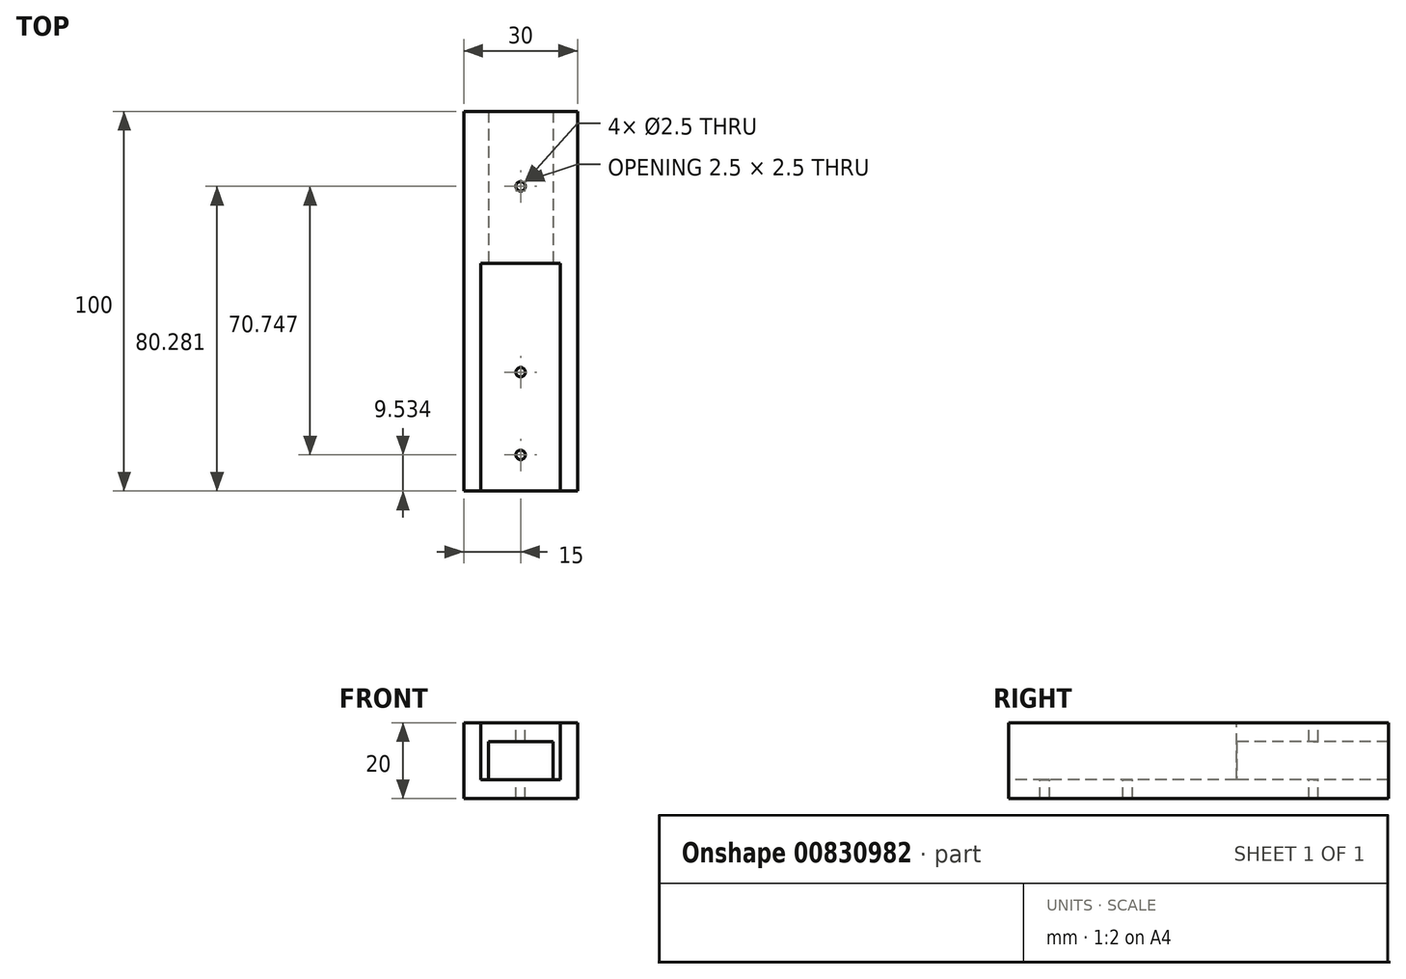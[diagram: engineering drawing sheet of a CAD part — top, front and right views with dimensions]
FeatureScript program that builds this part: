
annotation { "Feature Type Name" : "Feature", "Feature Type Description" : "" }
export const myFeature = defineFeature(function(context is Context, id is Id, definition is map)
    precondition{}
    {
        {
            var Q0;
            Q0=qCreatedBy(makeId("Top.planeOp"),FACE);
            var sketch = newSketch(context, id + "F0", { "sketchPlane" : qUnion([Q0])});
            skLineSegment(sketch, "E0.bottom", {"start": v(-15, 50) * mm, "end": v(15, 50) * mm});
            skLineSegment(sketch, "E0.top", {"start": v(-15, -50) * mm, "end": v(15, -50) * mm});
            skLineSegment(sketch, "E0.left", {"start": v(-15, 50) * mm, "end": v(-15, -50) * mm});
            skLineSegment(sketch, "E0.right", {"start": v(15, 50) * mm, "end": v(15, -50) * mm});
            skPoint(sketch, "E0.middle", {"position": v(0, 0) * mm});
            skSolve(sketch);
        }
        {
            var Q0;
            Q0 = qSketchRegion(id + "F0", true);
            extrude(context, id + "F1", {"entities" : qUnion([Q0]), "endBound" : BoundingType.SYMMETRIC, "depth" : 20 * mm, "offsetDistance" : 25 * mm});
        }
        {
            var Q0;
            Q0=makeQuery(id+"F1.opExtrude","SWEPT_FACE",FACE,{"disambiguationData":[OSD([sQuery(id+"F0.wireOp",EDGE,"E0.top")])]});
            var sketch = newSketch(context, id + "F2", { "sketchPlane" : qUnion([Q0])});
            skLineSegment(sketch, "E1.bottom", {"start": v(-8.5, 5) * mm, "end": v(8.5, 5) * mm});
            skLineSegment(sketch, "E1.top", {"start": v(-8.5, -5) * mm, "end": v(8.5, -5) * mm});
            skLineSegment(sketch, "E1.left", {"start": v(-8.5, 5) * mm, "end": v(-8.5, -5) * mm});
            skLineSegment(sketch, "E1.right", {"start": v(8.5, 5) * mm, "end": v(8.5, -5) * mm});
            skPoint(sketch, "E1.middle", {"position": v(0, 0) * mm});
            skLineSegment(sketch, "E2.top", {"start": v(-8.5, 10) * mm, "end": v(8.5, 10) * mm});
            skLineSegment(sketch, "E2.left", {"start": v(-8.5, 5) * mm, "end": v(-8.5, 10) * mm});
            skLineSegment(sketch, "E2.right", {"start": v(8.5, 5) * mm, "end": v(8.5, 10) * mm});
            skLineSegment(sketch, "E3.bottom", {"start": v(-8.5, -5) * mm, "end": v(-10.5, -5) * mm});
            skLineSegment(sketch, "E3.top", {"start": v(-8.5, 10) * mm, "end": v(-10.5, 10) * mm});
            skLineSegment(sketch, "E3.left", {"start": v(-8.5, -5) * mm, "end": v(-8.5, 10) * mm});
            skLineSegment(sketch, "E3.right", {"start": v(-10.5, -5) * mm, "end": v(-10.5, 10) * mm});
            skLineSegment(sketch, "E4.bottom", {"start": v(8.5, 10) * mm, "end": v(10.5, 10) * mm});
            skLineSegment(sketch, "E4.top", {"start": v(8.5, -5) * mm, "end": v(10.5, -5) * mm});
            skLineSegment(sketch, "E4.left", {"start": v(8.5, 10) * mm, "end": v(8.5, -5) * mm});
            skLineSegment(sketch, "E4.right", {"start": v(10.5, 10) * mm, "end": v(10.5, -5) * mm});
            skSolve(sketch);
        }
        {
            var Q0;
            Q0=makeQuery(id+"F2.imprint","IMPRINT",FACE,{"disambiguationData":[TD([[makeQuery(id+"F2.imprint","IMPRINT",EDGE,{"derivedFrom":sQuery(id+"F2.wireOp",EDGE,"E1.top")}),1.0]])]});
            extrude(context, id + "F3", {"entities" : qUnion([Q0]), "operationType" : NewBodyOperationType.REMOVE, "oppositeDirection" : true, "depth" : 200 * mm, "offsetDistance" : 25 * mm});
        }
        {
            var Q0;
            {var subQ3=sQuery(id+"F2.wireOp",EDGE,"E4.bottom");Q0=makeQuery(id+"F2.imprint","IMPRINT",FACE,{"disambiguationData":[TD([[makeQuery(id+"F2.imprint","IMPRINT",EDGE,{"derivedFrom":subQ3}),-1.0]])]});}
            var Q1;
            {var subQ3=sQuery(id+"F2.wireOp",EDGE,"E3.bottom");Q1=makeQuery(id+"F2.imprint","IMPRINT",FACE,{"disambiguationData":[TD([[makeQuery(id+"F2.imprint","IMPRINT",EDGE,{"derivedFrom":subQ3}),-1.0]])]});}
            var Q2;
            {var subQ0=sQuery(id+"F2.wireOp",EDGE,"E1.bottom");Q2=makeQuery(id+"F2.imprint","IMPRINT",FACE,{"disambiguationData":[TD([[makeQuery(id+"F2.imprint","IMPRINT",EDGE,{"derivedFrom":subQ0}),1.0]])]});}
            extrude(context, id + "F4", {"entities" : qUnion([Q0, Q1, Q2]), "operationType" : NewBodyOperationType.REMOVE, "oppositeDirection" : true, "depth" : 60 * mm, "offsetDistance" : 25 * mm});
        }
        {
            var Q0;
            Q0=makeQuery(id+"F3.boolean.opBoolean","COPY",FACE,{"derivedFrom":makeQuery(id+"F3.opExtrude","SWEPT_FACE",FACE,{"disambiguationData":[OSD([sQuery(id+"F2.wireOp",EDGE,"E1.top")])]})});
            var sketch = newSketch(context, id + "F5", { "sketchPlane" : qUnion([Q0])});
            skCircle(sketch, "E5", {"center": v(0, -18.69) * mm, "radius": 1.25 * mm});
            skCircle(sketch, "E6", {"center": v(0, -40.47) * mm, "radius": 1.25 * mm});
            skSolve(sketch);
        }
        {
            var Q0;
            Q0 = qSketchRegion(id + "F5", true);
            extrude(context, id + "F6", {"entities" : qUnion([Q0]), "operationType" : NewBodyOperationType.REMOVE, "oppositeDirection" : true, "depth" : 25 * mm, "offsetDistance" : 25 * mm});
        }
        {
            var Q0;
            Q0=makeQuery(id+"F1.opExtrude","CAP_FACE",FACE,{"disambiguationData":[OSD([sQuery(id+"F0.wireOp",EDGE,"E0.bottom"),sQuery(id+"F0.wireOp",EDGE,"E0.top"),sQuery(id+"F0.wireOp",EDGE,"E0.left"),sQuery(id+"F0.wireOp",EDGE,"E0.right")])],"isStart":false});
            var sketch = newSketch(context, id + "F7", { "sketchPlane" : qUnion([Q0])});
            skCircle(sketch, "E7", {"center": v(0, 30.28) * mm, "radius": 1.25 * mm});
            skSolve(sketch);
        }
        {
            var Q0;
            Q0 = qSketchRegion(id + "F7", true);
            extrude(context, id + "F8", {"entities" : qUnion([Q0]), "operationType" : NewBodyOperationType.REMOVE, "oppositeDirection" : true, "depth" : 25 * mm, "offsetDistance" : 25 * mm});
        }
    });
